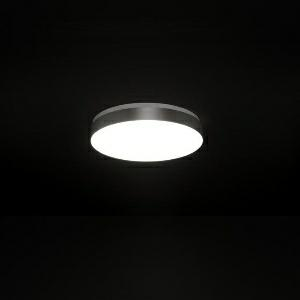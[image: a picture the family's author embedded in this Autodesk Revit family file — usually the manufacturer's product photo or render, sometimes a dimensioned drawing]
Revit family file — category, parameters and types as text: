
# Revit family: spectral_norea_norea-ra_306_1900_840_os_6a0f
name_source: partatom
category: Lighting Fixtures
revit_build: Autodesk Revit 2016 (Build: 20150220_1215(x64)
units: mm (PartAtom-declared; Revit-internal decimal feet)

## family parameters
Cut with Voids When Loaded = No
Host = Face
Light Source = No
Part Type = Normal
Room Calculation Point = No
Round Connector Dimension = Use Diameter
Shared = No

## types (1)
- SPECTRAL NOREA (1 x )
    Apparent Load = 0 VA
    Approval mark = CE
    CIE Flux Codes = 47 78 95 100 68
    Control Gear = Electronic transformer
    Default Elevation = 1800 mm
    Description = SPT0000145
NOREA surface-mounted luminaire

Design:
Round luminaire element comprising an acrylic opal glass panel in an anodised aluminium profile frame surround. The frame is fastened to the powder
coated steel body with a bayonet fixture with clip. The metal body accommodates the electrical components and electronic ballast. The LED module is formed as a round LED flat board and can be removed for installation or exchange using a key-hole screw connection. Plug-in electrical connection of the LED flat board. Luminaire with heat-resistant wiring Luminaire with heat-resistant wiring. Homogenous illumination of the light surface. Suitable for ceiling or wall mounting. Protection rating IP20, safety class I.

Colour:
Housing - similar to RAL 9016 white silk matt;
Frame - natural anodised
    Height = 78 mm  [stored 0.255906 ft]
    Lamp = 1 x
    Lamp count = 1
    Length = 306 mm
    Luminous efficacy = 0 lm/W
    Manufacturer = Ridi
    ModVariant = No
    Model = NOREA-RA 306/1900/840 OS
    Mounting Place = Ceiling
    Mounting Type = Surface mounted
    Number of Poles = 1
    OnlyDefault = Yes
    Power Factor = 1
    Product Name = SPECTRAL NOREA
    Product group = Ceiling mounted luminaire
    ProductGroupID = 3
    Protection Class = Protection class
    Protection Degree = IP 20
    RlxData = <blob elided: 29957 chars, md5=e44b18fe>
    Socket = socket
    Standby Power = 0 W
    System Light Flux = 0 lm
    System Power = 0 W
    Type Image = rundmittel01_-_kopie.jpg
    URL = http://reluxnet.relux.com
    VarID = 1
    Voltage = 0 V
    Weight = 0.00 kg
    Width = 0 mm  [stored 0 ft]

note: [stored X ft] marks values corroborated as IEEE doubles in the binary element streams (Revit-internal decimal feet)

## geometry (parser evidence)
native form markers: Sweep x14
no freeform markers — native parametric forms only
